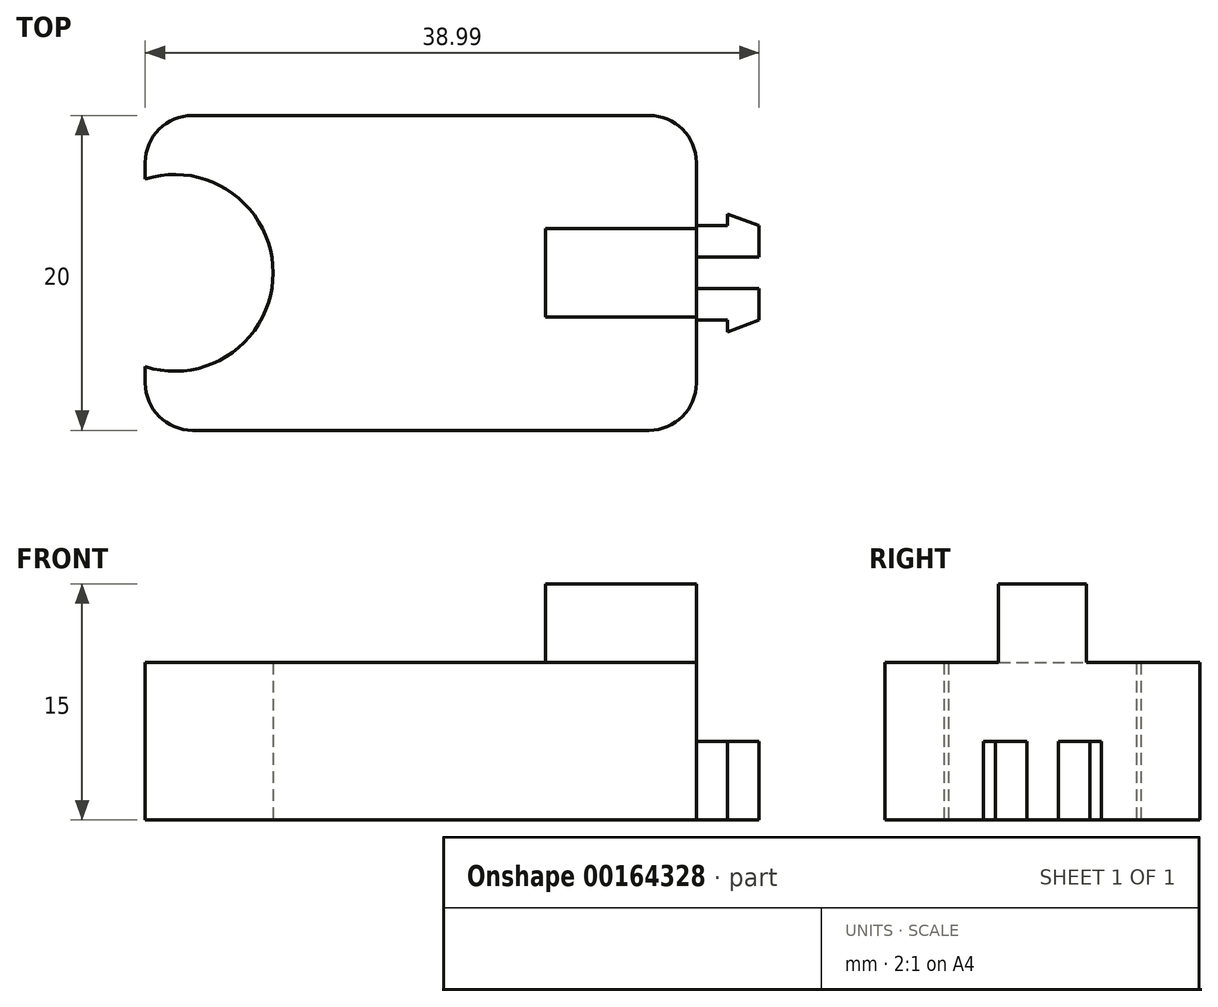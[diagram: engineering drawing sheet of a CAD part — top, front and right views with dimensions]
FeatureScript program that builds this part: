
annotation { "Feature Type Name" : "Feature", "Feature Type Description" : "" }
export const myFeature = defineFeature(function(context is Context, id is Id, definition is map)
    precondition{}
    {
        {
            var Q0;
            Q0=qCreatedBy(makeId("Top.planeOp"),FACE);
            var sketch = newSketch(context, id + "F0", { "sketchPlane" : qUnion([Q0])});
            skLineSegment(sketch, "E0.bottom", {"start": v(8.34, -2.13) * mm, "end": v(43.34, -2.13) * mm});
            skLineSegment(sketch, "E0.top", {"start": v(8.34, -22.13) * mm, "end": v(43.34, -22.13) * mm});
            skLineSegment(sketch, "E0.left", {"start": v(8.34, -2.13) * mm, "end": v(8.34, -22.13) * mm});
            skLineSegment(sketch, "E0.right", {"start": v(43.34, -2.13) * mm, "end": v(43.34, -22.13) * mm});
            skCircle(sketch, "E1", {"center": v(10.21, -12.13) * mm, "radius": 6.25 * mm});
            skPoint(sketch, "E1.centerSnap0", {"position": v(43.34, -12.13) * mm});
            skPoint(sketch, "E1.centerSnap1", {"position": v(25.84, -2.13) * mm});
            skLineSegment(sketch, "E2.bottom", {"start": v(33.77, -9.33) * mm, "end": v(43.34, -9.33) * mm});
            skLineSegment(sketch, "E2.top", {"start": v(33.77, -14.93) * mm, "end": v(43.34, -14.93) * mm});
            skLineSegment(sketch, "E2.left", {"start": v(33.77, -9.33) * mm, "end": v(33.77, -14.93) * mm});
            skLineSegment(sketch, "E2.right", {"start": v(43.34, -9.33) * mm, "end": v(43.34, -14.93) * mm});
            skLineSegment(sketch, "E3.bottom", {"start": v(43.33, -9.13) * mm, "end": v(47.33, -9.13) * mm});
            skLineSegment(sketch, "E3.top", {"start": v(43.33, -11.13) * mm, "end": v(47.33, -11.13) * mm});
            skLineSegment(sketch, "E3.right", {"start": v(47.33, -9.13) * mm, "end": v(47.33, -11.13) * mm});
            skLineSegment(sketch, "E4.bottom", {"start": v(43.33, -15.13) * mm, "end": v(47.33, -15.13) * mm});
            skLineSegment(sketch, "E4.top", {"start": v(43.33, -13.13) * mm, "end": v(47.33, -13.13) * mm});
            skLineSegment(sketch, "E4.right", {"start": v(47.33, -15.13) * mm, "end": v(47.33, -13.13) * mm});
            skLineSegment(sketch, "E5", {"start": v(47.33, -9.13) * mm, "end": v(45.33, -8.38) * mm});
            skLineSegment(sketch, "E6", {"start": v(45.33, -8.38) * mm, "end": v(45.33, -15.88) * mm});
            skLineSegment(sketch, "E7", {"start": v(45.33, -15.88) * mm, "end": v(47.33, -15.13) * mm});
            skPoint(sketch, "E8", {"position": v(45.33, -12.13) * mm});
            skPoint(sketch, "E9", {"position": v(44.4, -12.13) * mm});
            skLineSegment(sketch, "E10", {"start": v(44.03, -11.13) * mm, "end": v(44.03, -13.13) * mm});
            skSolve(sketch);
        }
        {
            var Q0;
            {var subQ1=sQuery(id+"F0.wireOp",EDGE,"E0.bottom");Q0=makeQuery(id+"F0.imprint","IMPRINT",FACE,{"disambiguationData":[TD([[makeQuery(id+"F0.imprint","IMPRINT",EDGE,{"derivedFrom":subQ1}),-1.0]])]});}
            var Q1;
            Q1=makeQuery(id+"F0.imprint","IMPRINT",FACE,{"disambiguationData":[TD([[makeQuery(id+"F0.imprint","IMPRINT",EDGE,{"derivedFrom":sQuery(id+"F0.wireOp",EDGE,"E2.bottom")}),-1.0]])]});
            extrude(context, id + "F1", {"entities" : qUnion([Q0, Q1]), "depth" : 10 * mm, "offsetDistance" : 25 * mm});
        }
        {
            var Q0;
            Q0=makeQuery(id+"F0.imprint","IMPRINT",FACE,{"disambiguationData":[TD([[makeQuery(id+"F0.imprint","IMPRINT",EDGE,{"derivedFrom":sQuery(id+"F0.wireOp",EDGE,"E2.bottom")}),-1.0]])]});
            extrude(context, id + "F2", {"entities" : qUnion([Q0]), "operationType" : NewBodyOperationType.ADD, "depth" : 15 * mm, "offsetDistance" : 25 * mm});
        }
        {
            var Q0;
            Q0=makeQuery(id+"F1.opExtrude","SWEPT_EDGE",EDGE,{"disambiguationData":[OSD([sQuery(id+"F0.wireOp",EDGE,"E0.top"),sQuery(id+"F0.wireOp",EDGE,"E0.left")])]});
            var Q1;
            Q1=makeQuery(id+"F1.opExtrude","SWEPT_EDGE",EDGE,{"disambiguationData":[OSD([sQuery(id+"F0.wireOp",EDGE,"E0.top"),sQuery(id+"F0.wireOp",EDGE,"E0.right")])]});
            var Q2;
            Q2=makeQuery(id+"F1.opExtrude","SWEPT_EDGE",EDGE,{"disambiguationData":[OSD([sQuery(id+"F0.wireOp",EDGE,"E0.bottom"),sQuery(id+"F0.wireOp",EDGE,"E0.right")])]});
            var Q3;
            Q3=makeQuery(id+"F1.opExtrude","SWEPT_EDGE",EDGE,{"disambiguationData":[OSD([sQuery(id+"F0.wireOp",EDGE,"E0.bottom"),sQuery(id+"F0.wireOp",EDGE,"E0.left")])]});
            fillet(context, id + "F3", {"entities" : qUnion([Q0, Q1, Q2, Q3]), "radius" : 3 * mm, "tangentPropagation" : true, "allowEdgeOverflow" : false});
        }
        {
            var Q0;
            {var subQ0=sQuery(id+"F0.wireOp",EDGE,"E3.bottom");var subQ1=sQuery(id+"F0.wireOp",EDGE,"E0.right");var subQ2=makeQuery(id+"F0.imprint","INTERSECT",VERTEX,{"derivedFrom":[subQ1,subQ0]});Q0=makeQuery(id+"F0.imprint","IMPRINT",FACE,{"disambiguationData":[TD([[makeQuery(id+"F0.imprint","IMPRINT",EDGE,{"disambiguationData":[TD([[subQ2,-1.0]])],"derivedFrom":subQ0}),-1.0]])]});}
            var Q1;
            {var subQ0=sQuery(id+"F0.wireOp",EDGE,"E3.right");Q1=makeQuery(id+"F0.imprint","IMPRINT",FACE,{"disambiguationData":[TD([[makeQuery(id+"F0.imprint","IMPRINT",EDGE,{"derivedFrom":subQ0}),-1.0]])]});}
            var Q2;
            {var subQ0=sQuery(id+"F0.wireOp",EDGE,"E5");Q2=makeQuery(id+"F0.imprint","IMPRINT",FACE,{"disambiguationData":[TD([[makeQuery(id+"F0.imprint","IMPRINT",EDGE,{"derivedFrom":subQ0}),1.0]])]});}
            var Q3;
            {var subQ0=sQuery(id+"F0.wireOp",EDGE,"E4.right");Q3=makeQuery(id+"F0.imprint","IMPRINT",FACE,{"disambiguationData":[TD([[makeQuery(id+"F0.imprint","IMPRINT",EDGE,{"derivedFrom":subQ0}),1.0]])]});}
            var Q4;
            {var subQ0=sQuery(id+"F0.wireOp",EDGE,"E7");Q4=makeQuery(id+"F0.imprint","IMPRINT",FACE,{"disambiguationData":[TD([[makeQuery(id+"F0.imprint","IMPRINT",EDGE,{"derivedFrom":subQ0}),1.0]])]});}
            var Q5;
            {var subQ4=sQuery(id+"F0.wireOp",EDGE,"E4.bottom");var subQ5=sQuery(id+"F0.wireOp",EDGE,"E0.right");var subQ6=makeQuery(id+"F0.imprint","INTERSECT",VERTEX,{"derivedFrom":[subQ5,subQ4]});Q5=makeQuery(id+"F0.imprint","IMPRINT",FACE,{"disambiguationData":[TD([[makeQuery(id+"F0.imprint","IMPRINT",EDGE,{"disambiguationData":[TD([[subQ6,-1.0]])],"derivedFrom":subQ4}),1.0]])]});}
            extrude(context, id + "F4", {"entities" : qUnion([Q0, Q1, Q2, Q3, Q4, Q5]), "operationType" : NewBodyOperationType.ADD, "depth" : 5 * mm, "offsetDistance" : 25 * mm});
        }
    });
